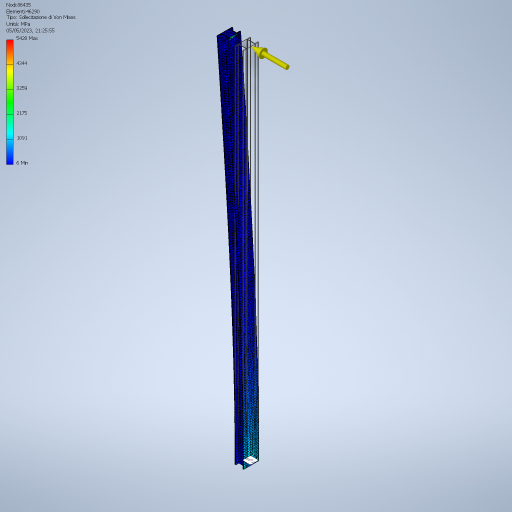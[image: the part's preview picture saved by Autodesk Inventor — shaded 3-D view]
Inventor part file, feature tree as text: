
AUTODESK INVENTOR PART (.ipt)
format: ipt  version: 2023 (Build 270158000, 158)  size: 342,528 bytes
history: native  units: mm
features: extrude x1, sketch x1
ambient origin geometry x8: Origin, YZ Plane, XZ Plane, XY Plane, X Axis, Y Axis, Z Axis, Center Point
bodies: Solido1 (feature_tree)
feature tree (2):
  extrude  "Estrusione1"  [1 undecoded]
  sketch  "Schizzo1"
note: 1 required parameter value undecoded (feature->parameter linkage not recoverable at this tier; creation-order binding heuristic only, values carry confidence <= 0.55)
